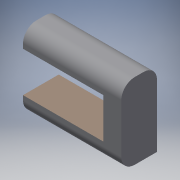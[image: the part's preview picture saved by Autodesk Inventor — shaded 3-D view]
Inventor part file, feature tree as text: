
AUTODESK INVENTOR PART (.ipt)
format: ipt  version: 2016 (Build 200138000, 138)  size: 103,424 bytes
history: native  units: mm
features: thicken_offset x1, fillet x1, sketch x1, other x1, extrude x1
ambient origin geometry x8: Origin, YZ Plane, XZ Plane, XY Plane, X Axis, Y Axis, Z Axis, Center Point
bodies: Solid1 (feature_tree)
feature tree (5):
  thicken_offset  "Thicken1"
  fillet  "Fillet1"  Radius=2.25mm
  sketch  "Sketch1"  dims[d2=2.0mm d3=0.0mm d4=1.0mm d5=1.0mm d6=0.75mm]
  other  "Srf1"
  extrude  "ExtrusionSrf1"  Depth=1.0mm
